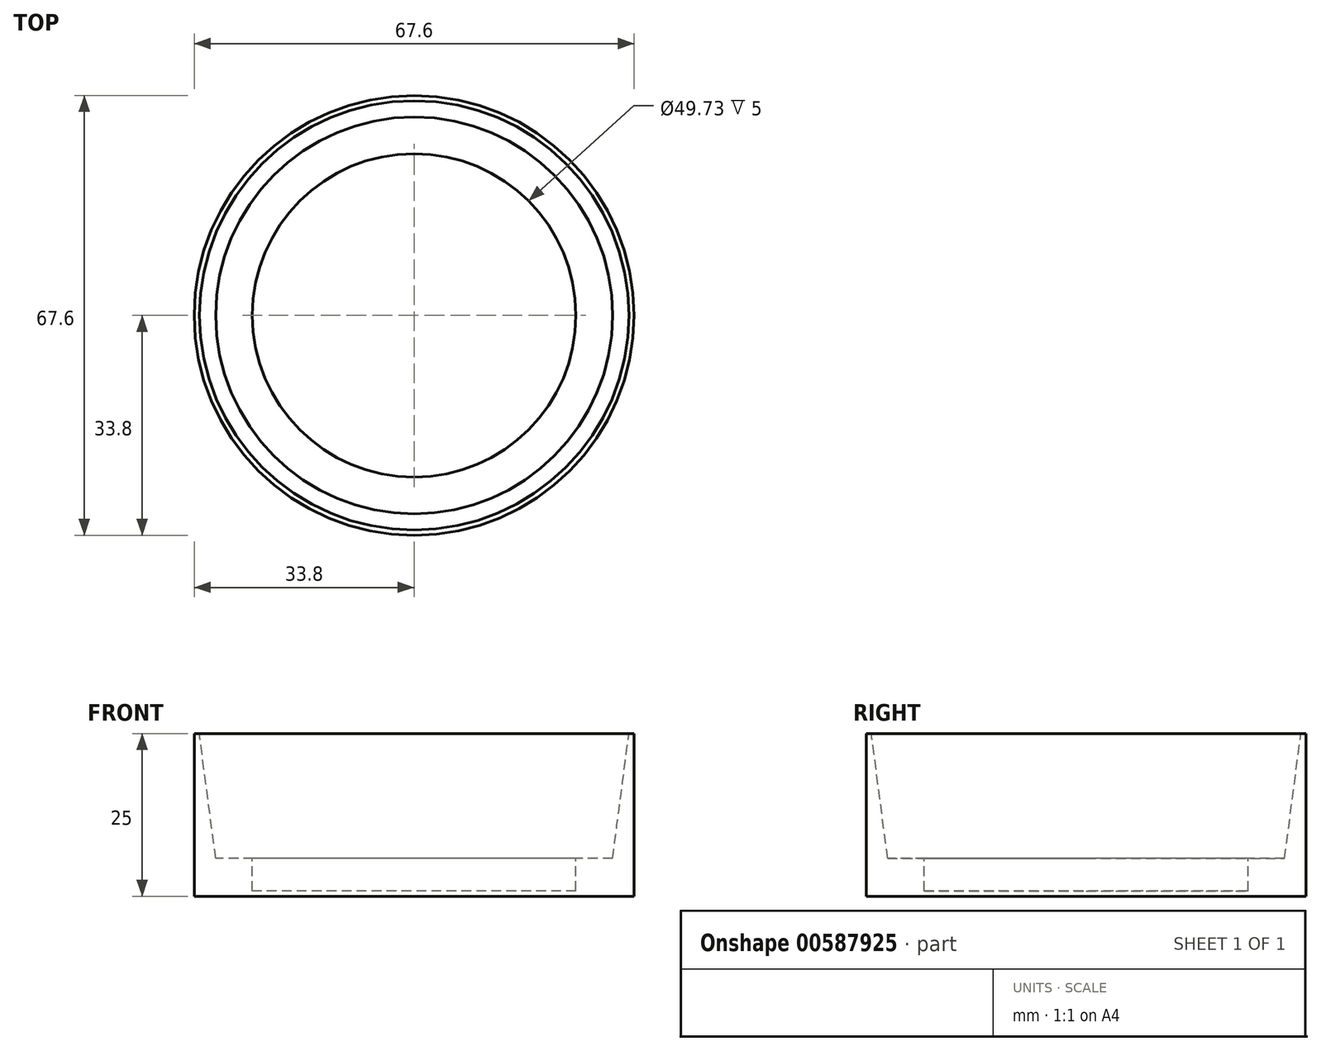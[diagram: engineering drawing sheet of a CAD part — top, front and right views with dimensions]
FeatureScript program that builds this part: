
annotation { "Feature Type Name" : "Feature", "Feature Type Description" : "" }
export const myFeature = defineFeature(function(context is Context, id is Id, definition is map)
    precondition{}
    {
        {
            var Q0;
            Q0=qCreatedBy(makeId("Right.planeOp"),FACE);
            var sketch = newSketch(context, id + "F0", { "sketchPlane" : qUnion([Q0])});
            skLineSegment(sketch, "E0", {"start": v(0, 0) * mm, "end": v(-33.8, 0) * mm});
            skLineSegment(sketch, "E1", {"start": v(-33.8, 0) * mm, "end": v(-33.8, 25) * mm});
            skLineSegment(sketch, "E2", {"start": v(-33.8, 25) * mm, "end": v(-33, 25) * mm});
            skLineSegment(sketch, "E3", {"start": v(-33, 25) * mm, "end": v(-31.63, 14.46) * mm});
            skLineSegment(sketch, "E4", {"start": v(0, 0.8) * mm, "end": v(0, 0) * mm});
            skPoint(sketch, "E5.orphan", {"position": v(-30.5, 5.8) * mm});
            skLineSegment(sketch, "E6", {"start": v(-24.87, 5.8) * mm, "end": v(-24.87, 4.88) * mm});
            skLineSegment(sketch, "E7", {"start": v(-24.87, 4.88) * mm, "end": v(-24.87, 0.8) * mm});
            skPoint(sketch, "E8.endSnap0", {"position": v(-16.9, 0) * mm});
            skLineSegment(sketch, "E9", {"start": v(0, 0.8) * mm, "end": v(-24.87, 0.8) * mm});
            skPoint(sketch, "E10.start.orphan", {"position": v(-22.67, 0) * mm});
            skLineSegment(sketch, "E11", {"start": v(-31.63, 14.46) * mm, "end": v(-30.5, 5.8) * mm});
            skLineSegment(sketch, "E12", {"start": v(-24.87, 5.8) * mm, "end": v(-30.5, 5.8) * mm});
            skSolve(sketch);
        }
        {
            var Q0;
            Q0=makeQuery(id+"F0.imprint","IMPRINT",FACE,{"disambiguationData":[TD([[makeQuery(id+"F0.imprint","IMPRINT",EDGE,{"derivedFrom":sQuery(id+"F0.wireOp",EDGE,"E0")}),-1.0]])]});
            var Q1;
            Q1=sQuery(id+"F0.wireOp",EDGE,"E4");
            revolve(context, id + "F1", {"entities" : qUnion([Q0]), "axis" : qUnion([Q1]), "revolveType" : RevolveType.FULL});
        }
    });
